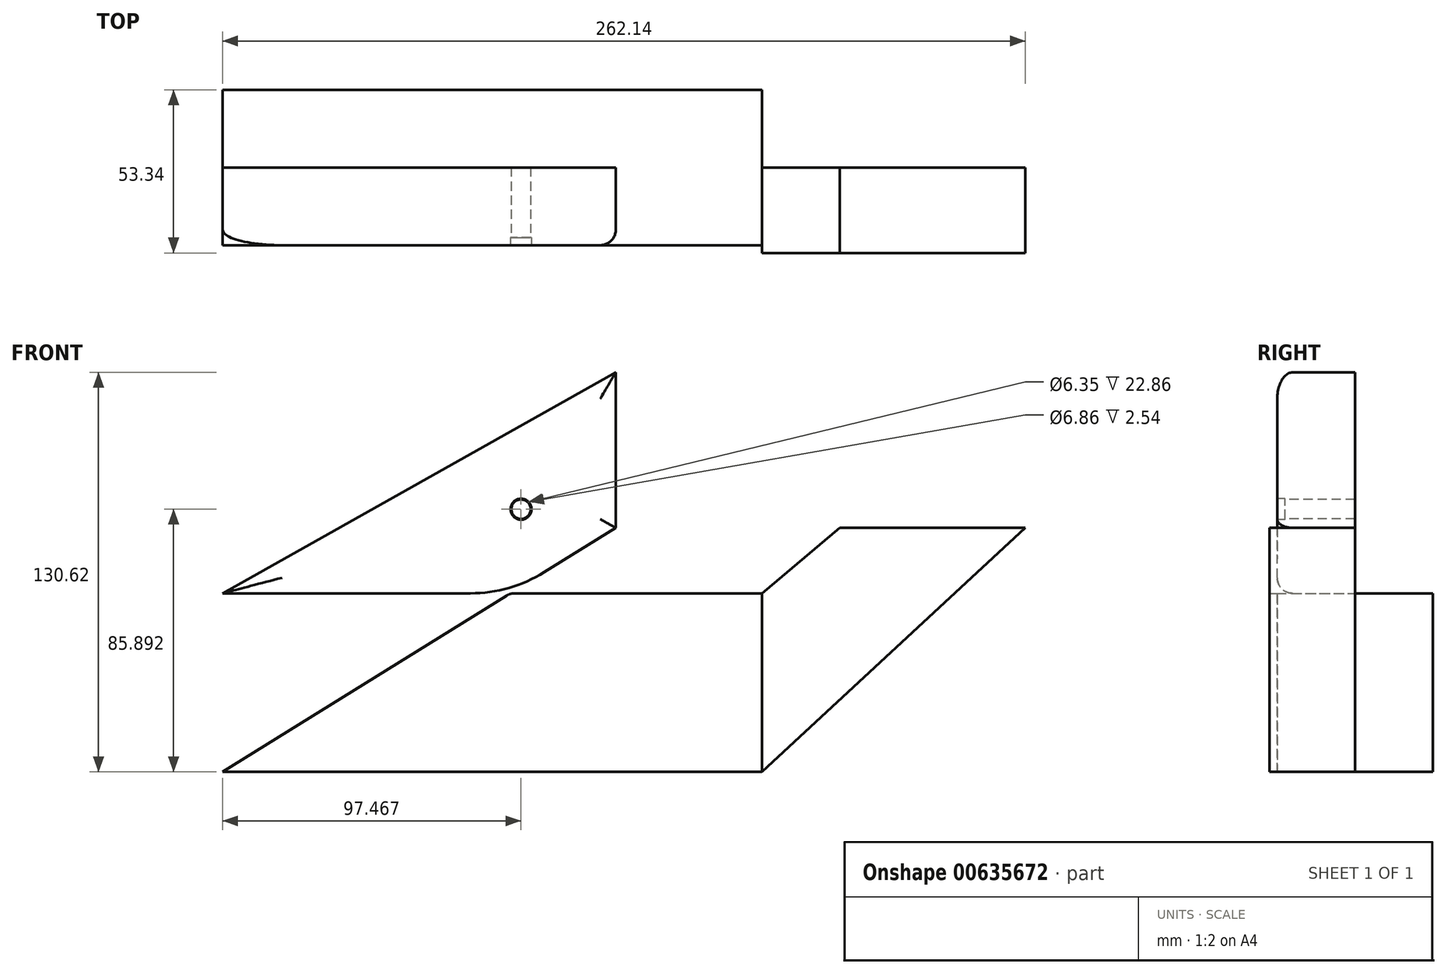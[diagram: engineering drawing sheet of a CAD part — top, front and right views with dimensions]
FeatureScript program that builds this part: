
annotation { "Feature Type Name" : "Feature", "Feature Type Description" : "" }
export const myFeature = defineFeature(function(context is Context, id is Id, definition is map)
    precondition{}
    {
        {
            var Q0;
            Q0=qCreatedBy(makeId("Front.planeOp"),FACE);
            var sketch = newSketch(context, id + "F0", { "sketchPlane" : qUnion([Q0])});
            skLineSegment(sketch, "E0.bottom", {"start": v(-88.05, -29.2) * mm, "end": v(88.05, -29.2) * mm});
            skLineSegment(sketch, "E0.top", {"start": v(-88.05, 29.2) * mm, "end": v(88.05, 29.2) * mm});
            skLineSegment(sketch, "E0.left", {"start": v(-88.05, -29.2) * mm, "end": v(-88.05, 29.2) * mm});
            skLineSegment(sketch, "E0.right", {"start": v(88.05, -29.2) * mm, "end": v(88.05, 29.2) * mm});
            skPoint(sketch, "E0.middle", {"position": v(0, 0) * mm});
            skLineSegment(sketch, "E1.bottom", {"start": v(40.35, 50.6) * mm, "end": v(174.1, 50.6) * mm});
            skLineSegment(sketch, "E1.top", {"start": v(40.35, 101.42) * mm, "end": v(174.1, 101.42) * mm});
            skLineSegment(sketch, "E1.left", {"start": v(40.35, 50.6) * mm, "end": v(40.35, 101.42) * mm});
            skLineSegment(sketch, "E1.right", {"start": v(174.1, 50.6) * mm, "end": v(174.1, 101.42) * mm});
            skPoint(sketch, "E1.middle", {"position": v(107.22, 76.01) * mm});
            skLineSegment(sketch, "E2", {"start": v(-88.05, 29.2) * mm, "end": v(40.35, 101.42) * mm});
            skLineSegment(sketch, "E3", {"start": v(40.35, 50.6) * mm, "end": v(-88.05, -29.2) * mm});
            skLineSegment(sketch, "E4", {"start": v(88.05, -29.2) * mm, "end": v(174.1, 50.6) * mm});
            skLineSegment(sketch, "E5", {"start": v(88.05, 29.2) * mm, "end": v(174.1, 101.42) * mm});
            skSolve(sketch);
        }
        {
            var Q0;
            {var subQ0=sQuery(id+"F0.wireOp",EDGE,"E0.bottom");Q0=makeQuery(id+"F0.imprint","IMPRINT",FACE,{"disambiguationData":[TD([[makeQuery(id+"F0.imprint","IMPRINT",EDGE,{"derivedFrom":subQ0}),1.0]])]});}
            extrude(context, id + "F1", {"entities" : qUnion([Q0]), "endBound" : BoundingType.SYMMETRIC, "depth" : 50.8 * mm, "offsetDistance" : 25.4 * mm});
        }
        {
            var Q0;
            {var subQ4=sQuery(id+"F0.wireOp",EDGE,"E1.left");Q0=makeQuery(id+"F0.imprint","IMPRINT",FACE,{"disambiguationData":[TD([[makeQuery(id+"F0.imprint","IMPRINT",EDGE,{"derivedFrom":subQ4}),1.0]])]});}
            extrude(context, id + "F2", {"entities" : qUnion([Q0]), "depth" : 25.4 * mm, "offsetDistance" : 25.4 * mm});
        }
        {
            var Q0;
            {var subQ0=sQuery(id+"F0.wireOp",EDGE,"E0.right");Q0=makeQuery(id+"F0.imprint","IMPRINT",FACE,{"disambiguationData":[TD([[makeQuery(id+"F0.imprint","IMPRINT",EDGE,{"derivedFrom":subQ0}),-1.0]])]});}
            extrude(context, id + "F3", {"entities" : qUnion([Q0]), "operationType" : NewBodyOperationType.ADD, "depth" : 27.94 * mm, "offsetDistance" : 25.4 * mm});
        }
        {
            var Q0;
            Q0=makeQuery(id+"F2.opExtrude","CAP_EDGE",EDGE,{"disambiguationData":[OSD([sQuery(id+"F0.wireOp",EDGE,"E2")])],"isStart":false});
            var Q1;
            Q1=makeQuery(id+"F2.opExtrude","CAP_EDGE",EDGE,{"disambiguationData":[OSD([sQuery(id+"F0.wireOp",EDGE,"E1.left")])],"isStart":false});
            var Q2;
            Q2=makeQuery(id+"F2.opExtrude","CAP_EDGE",EDGE,{"disambiguationData":[OSD([sQuery(id+"F0.wireOp",EDGE,"E3")])],"isStart":false});
            var Q3;
            Q3=makeQuery(id+"F2.opExtrude","CAP_EDGE",EDGE,{"disambiguationData":[OSD([sQuery(id+"F0.wireOp",EDGE,"E0.top")])],"isStart":false});
            fillet(context, id + "F4", {"entities" : qUnion([Q0, Q1, Q2, Q3]), "radius" : 5.08 * mm, "tangentPropagation" : true, "allowEdgeOverflow" : false});
        }
        {
            var Q0;
            Q0=makeQuery(id+"F1.opExtrude","SWEPT_EDGE",EDGE,{"disambiguationData":[OSD([sQuery(id+"F0.wireOp",EDGE,"E0.top"),sQuery(id+"F0.wireOp",EDGE,"E3")])]});
            fillet(context, id + "F5", {"entities" : qUnion([Q0]), "radius" : 5.08 * mm, "tangentPropagation" : true, "allowEdgeOverflow" : false});
        }
        {
            var Q0;
            Q0=makeQuery(id+"F2.opExtrude","SWEPT_EDGE",EDGE,{"disambiguationData":[OSD([sQuery(id+"F0.wireOp",EDGE,"E0.top"),sQuery(id+"F0.wireOp",EDGE,"E3")])]});
            fillet(context, id + "F6", {"entities" : qUnion([Q0]), "radius" : 45.72 * mm, "tangentPropagation" : true, "allowEdgeOverflow" : false});
        }
        {
            var Q0;
            Q0=makeQuery(id+"F2.opExtrude","CAP_FACE",FACE,{"disambiguationData":[OSD([sQuery(id+"F0.wireOp",EDGE,"E0.top"),sQuery(id+"F0.wireOp",EDGE,"E1.left"),sQuery(id+"F0.wireOp",EDGE,"E2"),sQuery(id+"F0.wireOp",EDGE,"E3")])],"isStart":false});
            var sketch = newSketch(context, id + "F7", { "sketchPlane" : qUnion([Q0])});
            skPoint(sketch, "E6", {"position": v(9.42, 56.7) * mm});
            skSolve(sketch);
        }
        {
            var Q0;
            Q0=sQuery(id+"F7.wireOp",VERTEX,"E6");
            var Q1;
            Q1=makeQuery(id+"F2.opExtrude","SWEPT_BODY",BODY,{"disambiguationData":[OSD([sQuery(id+"F0.wireOp",EDGE,"E0.top"),sQuery(id+"F0.wireOp",EDGE,"E1.left"),sQuery(id+"F0.wireOp",EDGE,"E2"),sQuery(id+"F0.wireOp",EDGE,"E3")])]});
            hole(context, id + "F8", {"style" : HoleStyle.C_BORE, "endStyle" : HoleEndStyle.THROUGH, "holeDiameter" : 6.35 * mm, "cBoreDiameter" : 6.86 * mm, "cBoreDepth" : 2.54 * mm, "majorDiameter" : 6.35 * mm, "isTappedThrough" : true, "tappedDepth" : 12.7 * mm, "tapClearance" : 3, "locations" : qUnion([Q0]), "scope" : qUnion([Q1])});
        }
    });
